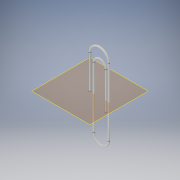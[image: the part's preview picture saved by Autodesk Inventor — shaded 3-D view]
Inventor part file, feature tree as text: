
AUTODESK INVENTOR PART (.ipt)
format: ipt  version: 2017 (Build 210142000, 142)  size: 126,464 bytes
history: native  units: in
note: dims shown in document units (in); Inventor stores cm internally (conversion verified against a paired STEP export)
features: sketch x2, plane x1, sweep x1
ambient origin geometry x8: Origin, YZ Plane, XZ Plane, XY Plane, X Axis, Y Axis, Z Axis, Center Point
bodies: Solid1 (feature_tree)
feature tree (4):
  sketch  "Sketch6"  dims[d1=0.5in d2=1.0in]
  plane  "Work Plane1"
  sweep  "Sweep1"
  sketch  "Sketch7"  dims[d3=0.222in d4=0.18in d5=0.55in d6=0.9in d7=0.14in d8=0.025in d9=0.0in d10=0.0in]
